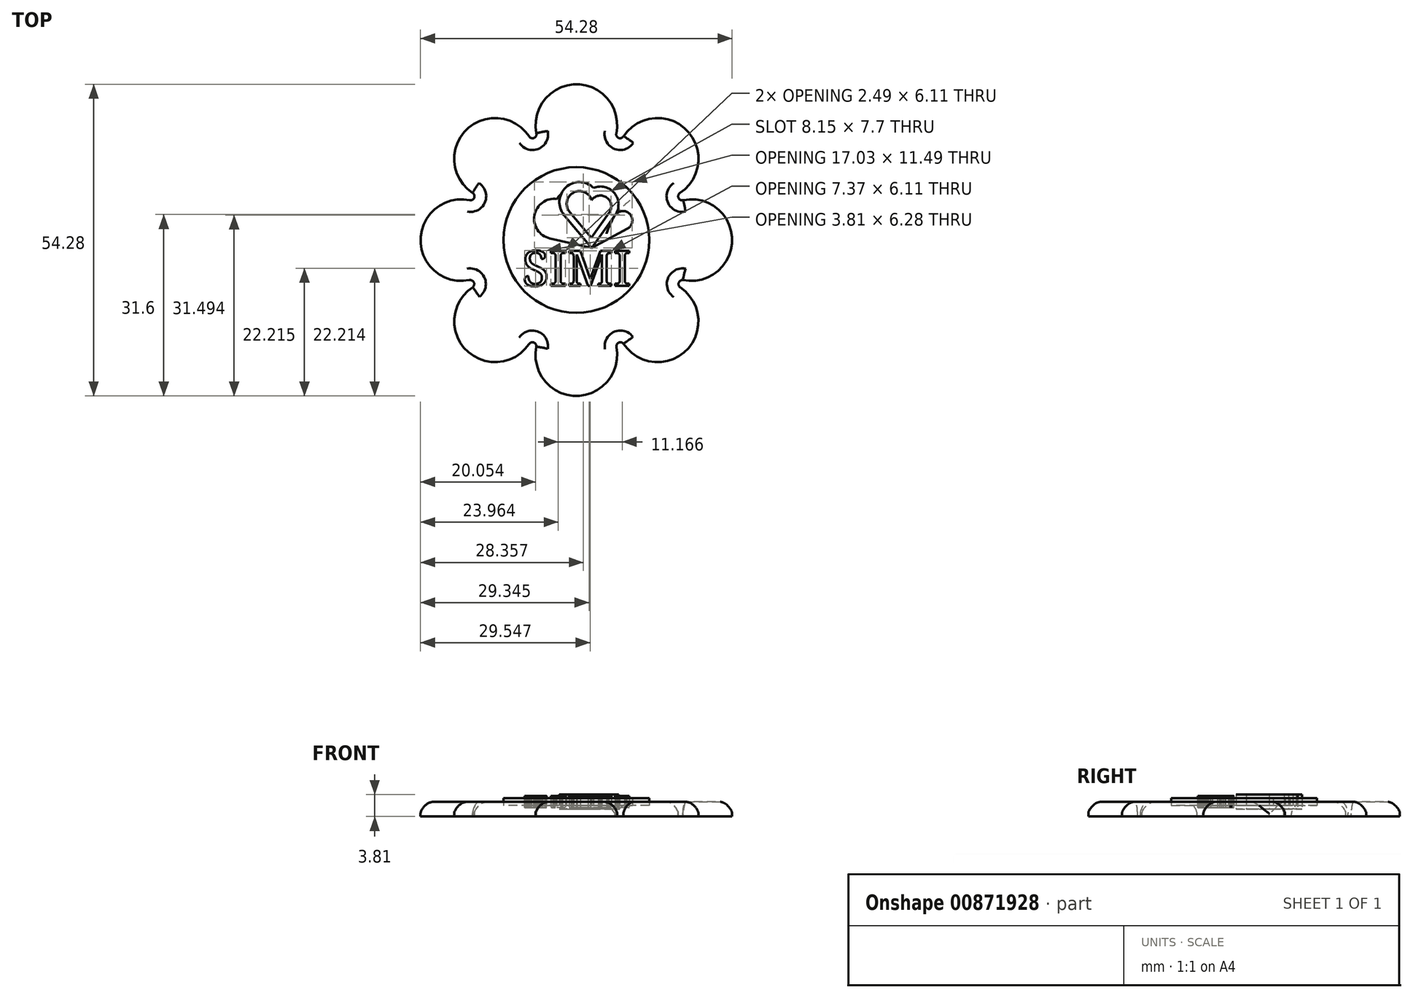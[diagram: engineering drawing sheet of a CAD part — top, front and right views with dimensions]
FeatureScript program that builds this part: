
annotation { "Feature Type Name" : "Feature", "Feature Type Description" : "" }
export const myFeature = defineFeature(function(context is Context, id is Id, definition is map)
    precondition{}
    {
        {
            var Q0;
            Q0=qCreatedBy(makeId("Top.planeOp"),FACE);
            var sketch = newSketch(context, id + "F0", { "sketchPlane" : qUnion([Q0])});
            skCircle(sketch, "E0", {"center": v(0, 0) * mm, "radius": 12.7 * mm});
            skArc(sketch, "E1", {"start": v(-6.97, 18.64) * mm, "mid": v(0.03, 27.14) * mm, "end": v(6.96, 18.57) * mm});
            skArc(sketch, "E2.1.0", {"start": v(-18.1, 8.25) * mm, "mid": v(-19.17, 19.22) * mm, "end": v(-8.2, 18.05) * mm});
            skArc(sketch, "E2.2.0", {"start": v(-18.64, -6.97) * mm, "mid": v(-27.14, 0.03) * mm, "end": v(-18.57, 6.96) * mm});
            skArc(sketch, "E2.3.0", {"start": v(-8.25, -18.1) * mm, "mid": v(-19.22, -19.17) * mm, "end": v(-18.05, -8.2) * mm});
            skArc(sketch, "E2.4.0", {"start": v(6.97, -18.64) * mm, "mid": v(-0.03, -27.14) * mm, "end": v(-6.96, -18.57) * mm});
            skArc(sketch, "E2.5.0", {"start": v(18.1, -8.25) * mm, "mid": v(19.17, -19.22) * mm, "end": v(8.2, -18.05) * mm});
            skArc(sketch, "E2.6.0", {"start": v(18.64, 6.97) * mm, "mid": v(27.14, -0.03) * mm, "end": v(18.57, -6.96) * mm});
            skArc(sketch, "E2.7.0", {"start": v(8.25, 18.1) * mm, "mid": v(19.22, 19.17) * mm, "end": v(18.05, 8.2) * mm});
            skArc(sketch, "E3", {"start": v(6.96, 18.57) * mm, "mid": v(7.4, 17.78) * mm, "end": v(8.25, 18.1) * mm});
            skArc(sketch, "E4", {"start": v(18.05, 8.2) * mm, "mid": v(17.8, 7.34) * mm, "end": v(18.64, 6.97) * mm});
            skArc(sketch, "E5", {"start": v(-8.2, 18.05) * mm, "mid": v(-7.34, 17.8) * mm, "end": v(-6.97, 18.64) * mm});
            skArc(sketch, "E6", {"start": v(-18.57, 6.96) * mm, "mid": v(-17.78, 7.4) * mm, "end": v(-18.1, 8.25) * mm});
            skArc(sketch, "E7", {"start": v(-18.64, -6.97) * mm, "mid": v(-17.86, -7.36) * mm, "end": v(-18.05, -8.2) * mm});
            skArc(sketch, "E8", {"start": v(-8.25, -18.1) * mm, "mid": v(-7.42, -17.84) * mm, "end": v(-6.96, -18.57) * mm});
            skArc(sketch, "E9", {"start": v(6.97, -18.64) * mm, "mid": v(7.36, -17.86) * mm, "end": v(8.2, -18.05) * mm});
            skArc(sketch, "E10", {"start": v(18.1, -8.25) * mm, "mid": v(17.84, -7.42) * mm, "end": v(18.57, -6.96) * mm});
            skText(sketch, "E11", { "text": "SIMI", "fontName": "NotoSerif-Regular.ttf"});
            skLineSegment(sketch, "E12", {"start": v(-1.16, 4.88) * mm, "end": v(2.6, 0.39) * mm});
            skLineSegment(sketch, "E13", {"start": v(2.6, 0.39) * mm, "end": v(5.73, 4.8) * mm});
            skArc(sketch, "E14", {"start": v(-1.16, 4.88) * mm, "mid": v(-0.52, 8.27) * mm, "end": v(2.67, 6.97) * mm});
            skArc(sketch, "E15", {"start": v(5.73, 4.8) * mm, "mid": v(5.29, 7.42) * mm, "end": v(2.67, 6.97) * mm});
            skLineSegment(sketch, "E16.0", {"start": v(-2.14, 4.37) * mm, "end": v(2.67, -1.4) * mm});
            skArc(sketch, "E16.1", {"start": v(-2.14, 4.37) * mm, "mid": v(-1.83, 9.18) * mm, "end": v(3, 9.1) * mm});
            skArc(sketch, "E16.2", {"start": v(6.76, 4.36) * mm, "mid": v(6.66, 8.14) * mm, "end": v(3, 9.1) * mm});
            skLineSegment(sketch, "E16.3", {"start": v(2.67, -1.4) * mm, "end": v(6.76, 4.36) * mm});
            skLineSegment(sketch, "E17.0", {"start": v(-4.64, 0.3) * mm, "end": v(2.67, -1.4) * mm});
            skArc(sketch, "E17.1", {"start": v(-4.64, 0.3) * mm, "mid": v(-7.3, 4.33) * mm, "end": v(-3.4, 7.17) * mm});
            skArc(sketch, "E17.2", {"start": v(2.46, 5.66) * mm, "mid": v(0.1, 8.62) * mm, "end": v(-3.4, 7.17) * mm});
            skLineSegment(sketch, "E17.3", {"start": v(2.67, -1.4) * mm, "end": v(2.46, 5.66) * mm});
            skLineSegment(sketch, "E18", {"start": v(2.67, -1.4) * mm, "end": v(8.9, 1.98) * mm});
            skArc(sketch, "E19", {"start": v(8.9, 1.98) * mm, "mid": v(9.33, 4.53) * mm, "end": v(6.76, 4.36) * mm});
            const initialGuessF0  = {"E11": [-0.0094, -0.00798, 1, 0, 0.00616]};
            skSetInitialGuess(sketch, initialGuessF0);
            skSolve(sketch);
        }
        {
            var Q0;
            Q0=makeQuery(id+"F0.imprint","IMPRINT",FACE,{"disambiguationData":[TD([[makeQuery(id+"F0.imprint","IMPRINT",EDGE,{"derivedFrom":sQuery(id+"F0.wireOp",EDGE,"E11.sketch_text.stroke-50")}),-1.0]])]});
            var Q1;
            {var subQ0=sQuery(id+"F0.wireOp",EDGE,"E16.3");Q1=makeQuery(id+"F0.imprint","IMPRINT",FACE,{"disambiguationData":[TD([[makeQuery(id+"F0.imprint","IMPRINT",EDGE,{"derivedFrom":subQ0}),-1.0]])]});}
            var Q2;
            {var subQ2=sQuery(id+"F0.wireOp",EDGE,"E16.0");Q2=makeQuery(id+"F0.imprint","IMPRINT",FACE,{"disambiguationData":[TD([[makeQuery(id+"F0.imprint","IMPRINT",EDGE,{"derivedFrom":subQ2}),-1.0]])]});}
            var Q3;
            {var subQ4=sQuery(id+"F0.wireOp",EDGE,"E15");Q3=makeQuery(id+"F0.imprint","IMPRINT",FACE,{"disambiguationData":[TD([[makeQuery(id+"F0.imprint","IMPRINT",EDGE,{"derivedFrom":subQ4}),-1.0]])]});}
            var Q4;
            {var subQ5=sQuery(id+"F0.wireOp",EDGE,"E12");Q4=makeQuery(id+"F0.imprint","IMPRINT",FACE,{"disambiguationData":[TD([[makeQuery(id+"F0.imprint","IMPRINT",EDGE,{"derivedFrom":subQ5}),1.0]])]});}
            var Q5;
            Q5=makeQuery(id+"F0.imprint","IMPRINT",FACE,{"disambiguationData":[TD([[makeQuery(id+"F0.imprint","IMPRINT",EDGE,{"derivedFrom":sQuery(id+"F0.wireOp",EDGE,"E11.sketch_text.stroke-127")}),-1.0]])]});
            var Q6;
            Q6=makeQuery(id+"F0.imprint","IMPRINT",FACE,{"disambiguationData":[TD([[makeQuery(id+"F0.imprint","IMPRINT",EDGE,{"derivedFrom":sQuery(id+"F0.wireOp",EDGE,"E0")}),1.0]])]});
            var Q7;
            Q7=makeQuery(id+"F0.imprint","IMPRINT",FACE,{"disambiguationData":[TD([[makeQuery(id+"F0.imprint","IMPRINT",EDGE,{"derivedFrom":sQuery(id+"F0.wireOp",EDGE,"E11.sketch_text.stroke-0")}),-1.0]])]});
            var Q8;
            Q8=makeQuery(id+"F0.imprint","IMPRINT",FACE,{"disambiguationData":[TD([[makeQuery(id+"F0.imprint","IMPRINT",EDGE,{"derivedFrom":sQuery(id+"F0.wireOp",EDGE,"E0")}),-1.0]])]});
            var Q9;
            {var subQ1=sQuery(id+"F0.wireOp",EDGE,"E12");Q9=makeQuery(id+"F0.imprint","IMPRINT",FACE,{"disambiguationData":[TD([[makeQuery(id+"F0.imprint","IMPRINT",EDGE,{"derivedFrom":subQ1}),-1.0]])]});}
            var Q10;
            Q10=makeQuery(id+"F0.imprint","IMPRINT",FACE,{"disambiguationData":[TD([[makeQuery(id+"F0.imprint","IMPRINT",EDGE,{"derivedFrom":sQuery(id+"F0.wireOp",EDGE,"E11.sketch_text.stroke-78")}),-1.0]])]});
            var Q11;
            {var subQ5=sQuery(id+"F0.wireOp",EDGE,"E15");Q11=makeQuery(id+"F0.imprint","IMPRINT",FACE,{"disambiguationData":[TD([[makeQuery(id+"F0.imprint","IMPRINT",EDGE,{"derivedFrom":subQ5}),1.0]])]});}
            extrude(context, id + "F1", {"entities" : qUnion([Q0, Q1, Q2, Q3, Q4, Q5, Q6, Q7, Q8, Q9, Q10, Q11]), "oppositeDirection" : true, "depth" : 2.54 * mm, "offsetDistance" : 25.4 * mm});
        }
        {
            var Q0;
            {var subQ4=sQuery(id+"F0.wireOp",EDGE,"E15");Q0=makeQuery(id+"F0.imprint","IMPRINT",FACE,{"disambiguationData":[TD([[makeQuery(id+"F0.imprint","IMPRINT",EDGE,{"derivedFrom":subQ4}),-1.0]])]});}
            var Q1;
            {var subQ1=sQuery(id+"F0.wireOp",EDGE,"E12");Q1=makeQuery(id+"F0.imprint","IMPRINT",FACE,{"disambiguationData":[TD([[makeQuery(id+"F0.imprint","IMPRINT",EDGE,{"derivedFrom":subQ1}),-1.0]])]});}
            extrude(context, id + "F2", {"entities" : qUnion([Q0, Q1]), "endBound" : BoundingType.SYMMETRIC, "depth" : 2.54 * mm, "offsetDistance" : 25.4 * mm});
        }
        {
            var Q0;
            {var subQ5=sQuery(id+"F0.wireOp",EDGE,"E15");Q0=makeQuery(id+"F0.imprint","IMPRINT",FACE,{"disambiguationData":[TD([[makeQuery(id+"F0.imprint","IMPRINT",EDGE,{"derivedFrom":subQ5}),1.0]])]});}
            var Q1;
            {var subQ5=sQuery(id+"F0.wireOp",EDGE,"E12");Q1=makeQuery(id+"F0.imprint","IMPRINT",FACE,{"disambiguationData":[TD([[makeQuery(id+"F0.imprint","IMPRINT",EDGE,{"derivedFrom":subQ5}),1.0]])]});}
            var Q2;
            Q2=makeQuery(id+"F0.imprint","IMPRINT",FACE,{"disambiguationData":[TD([[makeQuery(id+"F0.imprint","IMPRINT",EDGE,{"derivedFrom":sQuery(id+"F0.wireOp",EDGE,"E0")}),1.0]])]});
            extrude(context, id + "F3", {"entities" : qUnion([Q0, Q1, Q2]), "endBound" : BoundingType.SYMMETRIC, "depth" : 1.27 * mm, "offsetDistance" : 25.4 * mm});
        }
        {
            var Q0;
            Q0=makeQuery(id+"F0.imprint","IMPRINT",FACE,{"disambiguationData":[TD([[makeQuery(id+"F0.imprint","IMPRINT",EDGE,{"derivedFrom":sQuery(id+"F0.wireOp",EDGE,"E11.sketch_text.stroke-0")}),-1.0]])]});
            var Q1;
            Q1=makeQuery(id+"F0.imprint","IMPRINT",FACE,{"disambiguationData":[TD([[makeQuery(id+"F0.imprint","IMPRINT",EDGE,{"derivedFrom":sQuery(id+"F0.wireOp",EDGE,"E11.sketch_text.stroke-50")}),-1.0]])]});
            var Q2;
            Q2=makeQuery(id+"F0.imprint","IMPRINT",FACE,{"disambiguationData":[TD([[makeQuery(id+"F0.imprint","IMPRINT",EDGE,{"derivedFrom":sQuery(id+"F0.wireOp",EDGE,"E11.sketch_text.stroke-78")}),-1.0]])]});
            var Q3;
            Q3=makeQuery(id+"F0.imprint","IMPRINT",FACE,{"disambiguationData":[TD([[makeQuery(id+"F0.imprint","IMPRINT",EDGE,{"derivedFrom":sQuery(id+"F0.wireOp",EDGE,"E11.sketch_text.stroke-127")}),-1.0]])]});
            extrude(context, id + "F4", {"entities" : qUnion([Q0, Q1, Q2, Q3]), "endBound" : BoundingType.SYMMETRIC, "depth" : 2.03 * mm, "offsetDistance" : 25.4 * mm});
        }
        {
            var Q0;
            Q0=makeQuery(id+"F1.opExtrude","CAP_FACE",FACE,{"disambiguationData":[OSD([sQuery(id+"F0.wireOp",EDGE,"E1"),sQuery(id+"F0.wireOp",EDGE,"E2.1.0"),sQuery(id+"F0.wireOp",EDGE,"E2.2.0"),sQuery(id+"F0.wireOp",EDGE,"E2.3.0"),sQuery(id+"F0.wireOp",EDGE,"E2.4.0"),sQuery(id+"F0.wireOp",EDGE,"E2.5.0"),sQuery(id+"F0.wireOp",EDGE,"E2.6.0"),sQuery(id+"F0.wireOp",EDGE,"E2.7.0"),sQuery(id+"F0.wireOp",EDGE,"E3"),sQuery(id+"F0.wireOp",EDGE,"E4"),sQuery(id+"F0.wireOp",EDGE,"E5"),sQuery(id+"F0.wireOp",EDGE,"E6"),sQuery(id+"F0.wireOp",EDGE,"E7"),sQuery(id+"F0.wireOp",EDGE,"E8"),sQuery(id+"F0.wireOp",EDGE,"E9"),sQuery(id+"F0.wireOp",EDGE,"E10")])],"isStart":true});
            fillet(context, id + "F5", {"entities" : qUnion([Q0]), "radius" : 2.03 * mm, "rho" : .3, "crossSection" : FilletCrossSection.CONIC, "allowEdgeOverflow" : false});
        }
    });
